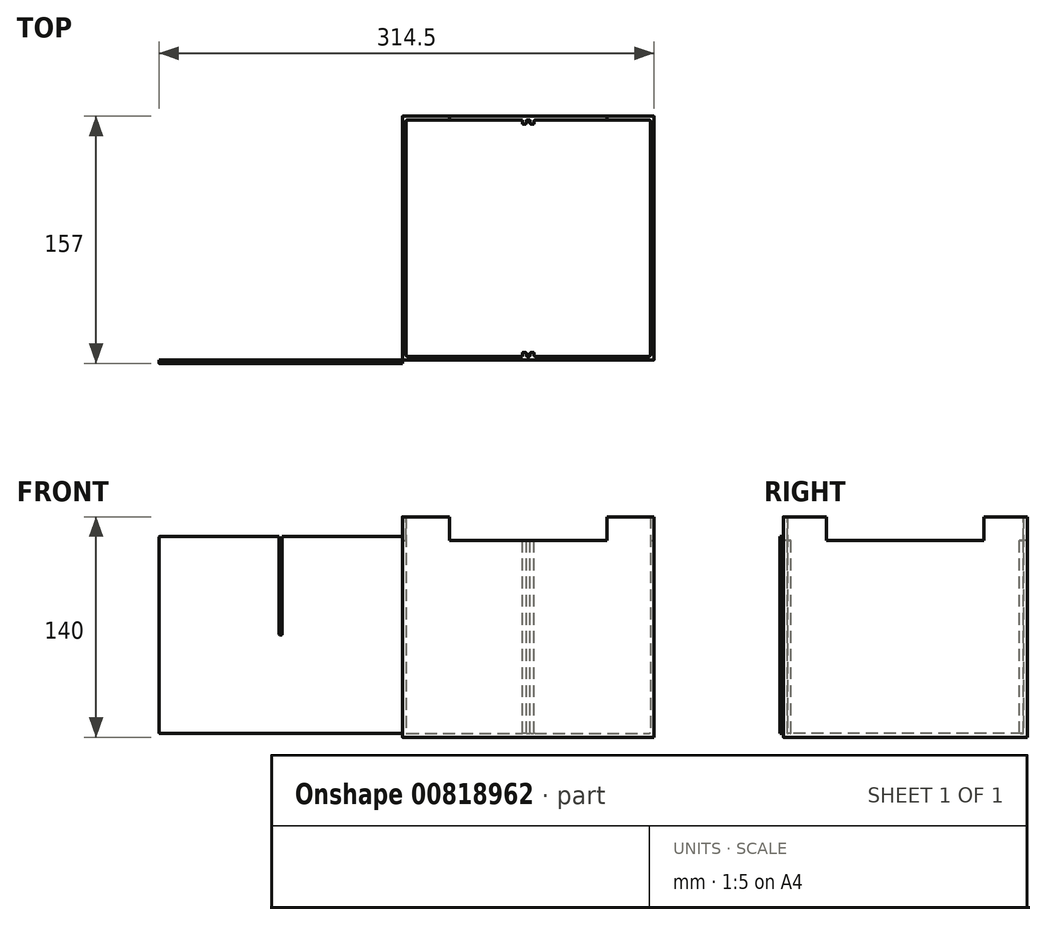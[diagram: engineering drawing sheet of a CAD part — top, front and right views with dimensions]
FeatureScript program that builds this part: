
annotation { "Feature Type Name" : "Feature", "Feature Type Description" : "" }
export const myFeature = defineFeature(function(context is Context, id is Id, definition is map)
    precondition{}
    {
        {
            var Q0;
            Q0=qCreatedBy(makeId("Top.planeOp"),FACE);
            var sketch = newSketch(context, id + "F0", { "sketchPlane" : qUnion([Q0])});
            skLineSegment(sketch, "E0.bottom", {"start": v(0, 0) * mm, "end": v(2.5, 0) * mm});
            skLineSegment(sketch, "E0.top", {"start": v(0, 155) * mm, "end": v(160, 155) * mm});
            skLineSegment(sketch, "E0.left", {"start": v(0, 0) * mm, "end": v(0, 155) * mm});
            skLineSegment(sketch, "E0.right", {"start": v(160, 0) * mm, "end": v(160, 155) * mm});
            skLineSegment(sketch, "E1.0", {"start": v(2.5, 152.5) * mm, "end": v(157.5, 152.5) * mm});
            skLineSegment(sketch, "E1.1", {"start": v(2.5, 2.5) * mm, "end": v(2.5, 152.5) * mm});
            skLineSegment(sketch, "E2", {"start": v(2.5, 2.5) * mm, "end": v(2.5, 0) * mm});
            skLineSegment(sketch, "E3.trimOffspring", {"start": v(157.5, 0) * mm, "end": v(160, 0) * mm});
            skLineSegment(sketch, "E4", {"start": v(157.5, 152.5) * mm, "end": v(157.5, 0) * mm});
            skLineSegment(sketch, "E5", {"start": v(2.5, 2.5) * mm, "end": v(157.5, 2.5) * mm});
            skLineSegment(sketch, "E6", {"start": v(2.5, 0) * mm, "end": v(157.5, 0) * mm});
            skSolve(sketch);
        }
        {
            var Q0;
            Q0=makeQuery(id+"F0.imprint","IMPRINT",FACE,{"disambiguationData":[TD([[makeQuery(id+"F0.imprint","IMPRINT",EDGE,{"derivedFrom":sQuery(id+"F0.wireOp",EDGE,"E0.bottom")}),1.0]])]});
            var Q1;
            Q1=makeQuery(id+"F0.imprint","IMPRINT",FACE,{"disambiguationData":[TD([[makeQuery(id+"F0.imprint","IMPRINT",EDGE,{"derivedFrom":sQuery(id+"F0.wireOp",EDGE,"E2")}),1.0]])]});
            extrude(context, id + "F1", {"entities" : qUnion([Q0, Q1]), "depth" : 137.5 * mm, "offsetDistance" : 25 * mm});
        }
        {
            var Q0;
            Q0=makeQuery(id+"F1.opExtrude","CAP_FACE",FACE,{"disambiguationData":[OSD([sQuery(id+"F0.wireOp",EDGE,"E0.bottom"),sQuery(id+"F0.wireOp",EDGE,"E0.top"),sQuery(id+"F0.wireOp",EDGE,"E0.left"),sQuery(id+"F0.wireOp",EDGE,"E0.right"),sQuery(id+"F0.wireOp",EDGE,"E1.0"),sQuery(id+"F0.wireOp",EDGE,"E1.1"),sQuery(id+"F0.wireOp",EDGE,"E2"),sQuery(id+"F0.wireOp",EDGE,"E3.trimOffspring"),sQuery(id+"F0.wireOp",EDGE,"E4")])],"isStart":true});
            var sketch = newSketch(context, id + "F2", { "sketchPlane" : qUnion([Q0])});
            skLineSegment(sketch, "E7.bottom", {"start": v(0, 0) * mm, "end": v(160, 0) * mm});
            skLineSegment(sketch, "E7.top", {"start": v(0, -155) * mm, "end": v(160, -155) * mm});
            skLineSegment(sketch, "E7.left", {"start": v(0, 0) * mm, "end": v(0, -155) * mm});
            skLineSegment(sketch, "E7.right", {"start": v(160, 0) * mm, "end": v(160, -155) * mm});
            skSolve(sketch);
        }
        {
            var Q0;
            Q0=makeQuery(id+"F2.imprint","IMPRINT",FACE,{"disambiguationData":[TD([[makeQuery(id+"F2.imprint","IMPRINT",EDGE,{"derivedFrom":makeQuery(id+"F1.opExtrude","CAP_EDGE",EDGE,{"disambiguationData":[OSD([sQuery(id+"F0.wireOp",EDGE,"E1.0")])],"isStart":true})}),1.0]])]});
            var Q1;
            Q1=makeQuery(id+"F2.imprint","IMPRINT",FACE,{"disambiguationData":[TD([[makeQuery(id+"F2.imprint","IMPRINT",EDGE,{"derivedFrom":sQuery(id+"F2.wireOp",EDGE,"E7.top")}),1.0]])]});
            extrude(context, id + "F3", {"entities" : qUnion([Q0, Q1]), "operationType" : NewBodyOperationType.ADD, "depth" : 2.5 * mm, "offsetDistance" : 25 * mm});
        }
        {
            var Q0;
            Q0=makeQuery(id+"F3.boolean.opBoolean","MERGE",EDGE,{"derivedFrom":[makeQuery(id+"F1.opExtrude","SWEPT_EDGE",EDGE,{"disambiguationData":[OSD([sQuery(id+"F0.wireOp",EDGE,"E0.top"),sQuery(id+"F0.wireOp",EDGE,"E0.left")])]}),makeQuery(id+"F3.opExtrude","SWEPT_EDGE",EDGE,{"disambiguationData":[OSD([sQuery(id+"F2.wireOp",EDGE,"E7.top"),sQuery(id+"F2.wireOp",EDGE,"E7.left")])]})]});
            var Q1;
            Q1=makeQuery(id+"F3.boolean.opBoolean","MERGE",EDGE,{"derivedFrom":[makeQuery(id+"F1.opExtrude","SWEPT_EDGE",EDGE,{"disambiguationData":[OSD([sQuery(id+"F0.wireOp",EDGE,"E0.top"),sQuery(id+"F0.wireOp",EDGE,"E0.right")])]}),makeQuery(id+"F3.opExtrude","SWEPT_EDGE",EDGE,{"disambiguationData":[OSD([sQuery(id+"F2.wireOp",EDGE,"E7.top"),sQuery(id+"F2.wireOp",EDGE,"E7.right")])]})]});
            var Q2;
            Q2=makeQuery(id+"F3.boolean.opBoolean","MERGE",EDGE,{"derivedFrom":[makeQuery(id+"F1.opExtrude","SWEPT_EDGE",EDGE,{"disambiguationData":[OSD([sQuery(id+"F0.wireOp",EDGE,"E0.right"),sQuery(id+"F0.wireOp",EDGE,"E3.trimOffspring")])]}),makeQuery(id+"F3.opExtrude","SWEPT_EDGE",EDGE,{"disambiguationData":[OSD([sQuery(id+"F2.wireOp",EDGE,"E7.bottom"),sQuery(id+"F2.wireOp",EDGE,"E7.right")])]})]});
            var Q3;
            Q3=makeQuery(id+"F3.boolean.opBoolean","MERGE",EDGE,{"derivedFrom":[makeQuery(id+"F1.opExtrude","SWEPT_EDGE",EDGE,{"disambiguationData":[OSD([sQuery(id+"F0.wireOp",EDGE,"E0.bottom"),sQuery(id+"F0.wireOp",EDGE,"E0.left")])]}),makeQuery(id+"F3.opExtrude","SWEPT_EDGE",EDGE,{"disambiguationData":[OSD([sQuery(id+"F2.wireOp",EDGE,"E7.bottom"),sQuery(id+"F2.wireOp",EDGE,"E7.left")])]})]});
            var Q4;
            Q4=makeQuery(id+"F1.opExtrude","SWEPT_EDGE",EDGE,{"disambiguationData":[OSD([sQuery(id+"F0.wireOp",EDGE,"E1.0"),sQuery(id+"F0.wireOp",EDGE,"E1.1")])]});
            var Q5;
            Q5=makeQuery(id+"F1.opExtrude","SWEPT_EDGE",EDGE,{"disambiguationData":[OSD([sQuery(id+"F0.wireOp",EDGE,"E1.0"),sQuery(id+"F0.wireOp",EDGE,"E4")])]});
            var Q6;
            Q6=makeQuery(id+"F1.opExtrude","SWEPT_EDGE",EDGE,{"disambiguationData":[OSD([sQuery(id+"F0.wireOp",EDGE,"E4"),sQuery(id+"F0.wireOp",EDGE,"E5")])]});
            var Q7;
            Q7=makeQuery(id+"F1.opExtrude","SWEPT_EDGE",EDGE,{"disambiguationData":[OSD([sQuery(id+"F0.wireOp",EDGE,"E1.1"),sQuery(id+"F0.wireOp",EDGE,"E2"),sQuery(id+"F0.wireOp",EDGE,"E5")])]});
            fillet(context, id + "F4", {"entities" : qUnion([Q0, Q1, Q2, Q3, Q4, Q5, Q6, Q7]), "radius" : 0.5 * mm, "tangentPropagation" : true, "allowEdgeOverflow" : false});
        }
        {
            var Q0;
            Q0=makeQuery(id+"F1.opExtrude","CAP_FACE",FACE,{"disambiguationData":[OSD([sQuery(id+"F0.wireOp",EDGE,"E0.bottom"),sQuery(id+"F0.wireOp",EDGE,"E0.top"),sQuery(id+"F0.wireOp",EDGE,"E0.left"),sQuery(id+"F0.wireOp",EDGE,"E0.right"),sQuery(id+"F0.wireOp",EDGE,"E1.0"),sQuery(id+"F0.wireOp",EDGE,"E1.1"),sQuery(id+"F0.wireOp",EDGE,"E3.trimOffspring"),sQuery(id+"F0.wireOp",EDGE,"E4"),sQuery(id+"F0.wireOp",EDGE,"E5"),sQuery(id+"F0.wireOp",EDGE,"E6")])],"isStart":false});
            var sketch = newSketch(context, id + "F5", { "sketchPlane" : qUnion([Q0])});
            skPoint(sketch, "E8", {"position": v(0, 77.5) * mm});
            skPoint(sketch, "E9", {"position": v(2.5, 77.5) * mm});
            skLineSegment(sketch, "E10.bottom", {"start": v(5, 78.75) * mm, "end": v(0, 78.75) * mm});
            skLineSegment(sketch, "E10.top", {"start": v(5, 76.25) * mm, "end": v(0, 76.25) * mm});
            skLineSegment(sketch, "E10.left", {"start": v(5, 78.75) * mm, "end": v(5, 76.25) * mm});
            skLineSegment(sketch, "E10.right", {"start": v(0, 78.75) * mm, "end": v(0, 76.25) * mm});
            skLineSegment(sketch, "E11.bottom", {"start": v(5, 78.75) * mm, "end": v(2.5, 78.75) * mm});
            skLineSegment(sketch, "E11.top", {"start": v(5, 81.25) * mm, "end": v(2.5, 81.25) * mm});
            skLineSegment(sketch, "E11.left", {"start": v(5, 78.75) * mm, "end": v(5, 81.25) * mm});
            skLineSegment(sketch, "E11.right", {"start": v(2.5, 78.75) * mm, "end": v(2.5, 81.25) * mm});
            skLineSegment(sketch, "E12.bottom", {"start": v(5, 76.25) * mm, "end": v(2.5, 76.25) * mm});
            skLineSegment(sketch, "E12.top", {"start": v(5, 73.75) * mm, "end": v(2.5, 73.75) * mm});
            skLineSegment(sketch, "E12.left", {"start": v(5, 76.25) * mm, "end": v(5, 73.75) * mm});
            skLineSegment(sketch, "E12.right", {"start": v(2.5, 76.25) * mm, "end": v(2.5, 73.75) * mm});
            skPoint(sketch, "E13", {"position": v(80, 152.5) * mm});
            skPoint(sketch, "E14", {"position": v(80, 155) * mm});
            skPoint(sketch, "E15", {"position": v(157.5, 77.5) * mm});
            skPoint(sketch, "E16", {"position": v(160, 77.5) * mm});
            skLineSegment(sketch, "E17.bottom", {"start": v(160, 78.75) * mm, "end": v(155, 78.75) * mm});
            skLineSegment(sketch, "E17.top", {"start": v(160, 76.25) * mm, "end": v(155, 76.25) * mm});
            skLineSegment(sketch, "E17.left", {"start": v(160, 78.75) * mm, "end": v(160, 76.25) * mm});
            skLineSegment(sketch, "E17.right", {"start": v(155, 78.75) * mm, "end": v(155, 76.25) * mm});
            skLineSegment(sketch, "E18.bottom", {"start": v(155, 78.75) * mm, "end": v(157.5, 78.75) * mm});
            skLineSegment(sketch, "E18.top", {"start": v(155, 81.25) * mm, "end": v(157.5, 81.25) * mm});
            skLineSegment(sketch, "E18.left", {"start": v(155, 78.75) * mm, "end": v(155, 81.25) * mm});
            skLineSegment(sketch, "E18.right", {"start": v(157.5, 78.75) * mm, "end": v(157.5, 81.25) * mm});
            skLineSegment(sketch, "E19.bottom", {"start": v(155, 76.25) * mm, "end": v(157.5, 76.25) * mm});
            skLineSegment(sketch, "E19.top", {"start": v(155, 73.75) * mm, "end": v(157.5, 73.75) * mm});
            skLineSegment(sketch, "E19.left", {"start": v(155, 76.25) * mm, "end": v(155, 73.75) * mm});
            skLineSegment(sketch, "E19.right", {"start": v(157.5, 76.25) * mm, "end": v(157.5, 73.75) * mm});
            skLineSegment(sketch, "E20.bottom", {"start": v(81.25, 155) * mm, "end": v(78.75, 155) * mm});
            skLineSegment(sketch, "E20.top", {"start": v(81.25, 150) * mm, "end": v(78.75, 150) * mm});
            skLineSegment(sketch, "E20.left", {"start": v(81.25, 155) * mm, "end": v(81.25, 150) * mm});
            skLineSegment(sketch, "E20.right", {"start": v(78.75, 155) * mm, "end": v(78.75, 150) * mm});
            skLineSegment(sketch, "E21.bottom", {"start": v(78.75, 150) * mm, "end": v(76.25, 150) * mm});
            skLineSegment(sketch, "E21.top", {"start": v(78.75, 152.5) * mm, "end": v(76.25, 152.5) * mm});
            skLineSegment(sketch, "E21.left", {"start": v(78.75, 150) * mm, "end": v(78.75, 152.5) * mm});
            skLineSegment(sketch, "E21.right", {"start": v(76.25, 150) * mm, "end": v(76.25, 152.5) * mm});
            skLineSegment(sketch, "E22.bottom", {"start": v(81.25, 150) * mm, "end": v(83.75, 150) * mm});
            skLineSegment(sketch, "E22.top", {"start": v(81.25, 152.5) * mm, "end": v(83.75, 152.5) * mm});
            skLineSegment(sketch, "E22.left", {"start": v(81.25, 150) * mm, "end": v(81.25, 152.5) * mm});
            skLineSegment(sketch, "E22.right", {"start": v(83.75, 150) * mm, "end": v(83.75, 152.5) * mm});
            skPoint(sketch, "E23", {"position": v(80, 2.5) * mm});
            skPoint(sketch, "E24", {"position": v(80, 0) * mm});
            skLineSegment(sketch, "E25.bottom", {"start": v(81.25, 0) * mm, "end": v(78.75, 0) * mm});
            skLineSegment(sketch, "E25.top", {"start": v(81.25, 5) * mm, "end": v(78.75, 5) * mm});
            skLineSegment(sketch, "E25.left", {"start": v(81.25, 0) * mm, "end": v(81.25, 5) * mm});
            skLineSegment(sketch, "E25.right", {"start": v(78.75, 0) * mm, "end": v(78.75, 5) * mm});
            skLineSegment(sketch, "E26.bottom", {"start": v(78.75, 5) * mm, "end": v(76.25, 5) * mm});
            skLineSegment(sketch, "E26.top", {"start": v(78.75, 2.5) * mm, "end": v(76.25, 2.5) * mm});
            skLineSegment(sketch, "E26.left", {"start": v(78.75, 5) * mm, "end": v(78.75, 2.5) * mm});
            skLineSegment(sketch, "E26.right", {"start": v(76.25, 5) * mm, "end": v(76.25, 2.5) * mm});
            skLineSegment(sketch, "E27.bottom", {"start": v(81.25, 5) * mm, "end": v(83.75, 5) * mm});
            skLineSegment(sketch, "E27.top", {"start": v(81.25, 2.5) * mm, "end": v(83.75, 2.5) * mm});
            skLineSegment(sketch, "E27.left", {"start": v(81.25, 5) * mm, "end": v(81.25, 2.5) * mm});
            skLineSegment(sketch, "E27.right", {"start": v(83.75, 5) * mm, "end": v(83.75, 2.5) * mm});
            skSolve(sketch);
        }
        {
            var Q0;
            Q0=makeQuery(id+"F5.imprint","IMPRINT",FACE,{"disambiguationData":[TD([[makeQuery(id+"F5.imprint","IMPRINT",EDGE,{"derivedFrom":sQuery(id+"F5.wireOp",EDGE,"E11.bottom")}),-1.0]])]});
            var Q1;
            Q1=makeQuery(id+"F5.imprint","IMPRINT",FACE,{"disambiguationData":[TD([[makeQuery(id+"F5.imprint","IMPRINT",EDGE,{"derivedFrom":sQuery(id+"F5.wireOp",EDGE,"E12.bottom")}),1.0]])]});
            var Q2;
            Q2=makeQuery(id+"F5.imprint","IMPRINT",FACE,{"disambiguationData":[TD([[makeQuery(id+"F5.imprint","IMPRINT",EDGE,{"derivedFrom":sQuery(id+"F5.wireOp",EDGE,"E26.bottom")}),1.0]])]});
            var Q3;
            Q3=makeQuery(id+"F5.imprint","IMPRINT",FACE,{"disambiguationData":[TD([[makeQuery(id+"F5.imprint","IMPRINT",EDGE,{"derivedFrom":sQuery(id+"F5.wireOp",EDGE,"E27.bottom")}),-1.0]])]});
            var Q4;
            Q4=makeQuery(id+"F5.imprint","IMPRINT",FACE,{"disambiguationData":[TD([[makeQuery(id+"F5.imprint","IMPRINT",EDGE,{"derivedFrom":sQuery(id+"F5.wireOp",EDGE,"E18.bottom")}),1.0]])]});
            var Q5;
            Q5=makeQuery(id+"F5.imprint","IMPRINT",FACE,{"disambiguationData":[TD([[makeQuery(id+"F5.imprint","IMPRINT",EDGE,{"derivedFrom":sQuery(id+"F5.wireOp",EDGE,"E19.bottom")}),-1.0]])]});
            var Q6;
            Q6=makeQuery(id+"F5.imprint","IMPRINT",FACE,{"disambiguationData":[TD([[makeQuery(id+"F5.imprint","IMPRINT",EDGE,{"derivedFrom":sQuery(id+"F5.wireOp",EDGE,"E22.bottom")}),1.0]])]});
            var Q7;
            Q7=makeQuery(id+"F5.imprint","IMPRINT",FACE,{"disambiguationData":[TD([[makeQuery(id+"F5.imprint","IMPRINT",EDGE,{"derivedFrom":sQuery(id+"F5.wireOp",EDGE,"E21.bottom")}),-1.0]])]});
            var Q8;
            Q8=makeQuery(id+"F3.opExtrude","CAP_FACE",FACE,{"disambiguationData":[OSD([sQuery(id+"F2.wireOp",EDGE,"E7.bottom"),sQuery(id+"F2.wireOp",EDGE,"E7.top"),sQuery(id+"F2.wireOp",EDGE,"E7.left"),sQuery(id+"F2.wireOp",EDGE,"E7.right")])],"isStart":true});
            extrude(context, id + "F6", {"entities" : qUnion([Q0, Q1, Q2, Q3, Q4, Q5, Q6, Q7]), "operationType" : NewBodyOperationType.ADD, "endBound" : BoundingType.UP_TO_SURFACE, "oppositeDirection" : true, "depth" : 25 * mm, "endBoundEntityFace" : qUnion([Q8]), "offsetDistance" : 25 * mm});
        }
        {
            var Q0;
            Q0=makeQuery(id+"F6.opExtrude","SWEPT_EDGE",EDGE,{"disambiguationData":[OSD([sQuery(id+"F5.wireOp",EDGE,"E11.top"),sQuery(id+"F5.wireOp",EDGE,"E11.left")])]});
            var Q1;
            Q1=makeQuery(id+"F6.opExtrude","SWEPT_EDGE",EDGE,{"disambiguationData":[OSD([sQuery(id+"F5.wireOp",EDGE,"E10.left"),sQuery(id+"F5.wireOp",EDGE,"E11.bottom"),sQuery(id+"F5.wireOp",EDGE,"E11.left")])]});
            var Q2;
            Q2=makeQuery(id+"F6.opExtrude","SWEPT_EDGE",EDGE,{"disambiguationData":[OSD([sQuery(id+"F0.wireOp",EDGE,"E1.1"),sQuery(id+"F5.wireOp",EDGE,"E10.bottom"),sQuery(id+"F5.wireOp",EDGE,"E11.bottom"),sQuery(id+"F5.wireOp",EDGE,"E11.right")])]});
            var Q3;
            Q3=makeQuery(id+"F6.opExtrude","SWEPT_EDGE",EDGE,{"disambiguationData":[OSD([sQuery(id+"F0.wireOp",EDGE,"E1.1"),sQuery(id+"F5.wireOp",EDGE,"E10.top"),sQuery(id+"F5.wireOp",EDGE,"E12.bottom"),sQuery(id+"F5.wireOp",EDGE,"E12.right")])]});
            var Q4;
            Q4=makeQuery(id+"F6.opExtrude","SWEPT_EDGE",EDGE,{"disambiguationData":[OSD([sQuery(id+"F5.wireOp",EDGE,"E10.left"),sQuery(id+"F5.wireOp",EDGE,"E12.bottom"),sQuery(id+"F5.wireOp",EDGE,"E12.left")])]});
            var Q5;
            Q5=makeQuery(id+"F6.opExtrude","SWEPT_EDGE",EDGE,{"disambiguationData":[OSD([sQuery(id+"F5.wireOp",EDGE,"E12.top"),sQuery(id+"F5.wireOp",EDGE,"E12.left")])]});
            var Q6;
            Q6=makeQuery(id+"F6.opExtrude","SWEPT_EDGE",EDGE,{"disambiguationData":[OSD([sQuery(id+"F0.wireOp",EDGE,"E1.1"),sQuery(id+"F5.wireOp",EDGE,"E12.top"),sQuery(id+"F5.wireOp",EDGE,"E12.right")])]});
            var Q7;
            Q7=makeQuery(id+"F6.opExtrude","SWEPT_EDGE",EDGE,{"disambiguationData":[OSD([sQuery(id+"F0.wireOp",EDGE,"E1.1"),sQuery(id+"F5.wireOp",EDGE,"E11.top"),sQuery(id+"F5.wireOp",EDGE,"E11.right")])]});
            var Q8;
            Q8=makeQuery(id+"F6.opExtrude","SWEPT_EDGE",EDGE,{"disambiguationData":[OSD([sQuery(id+"F5.wireOp",EDGE,"E21.bottom"),sQuery(id+"F5.wireOp",EDGE,"E21.right")])]});
            var Q9;
            Q9=makeQuery(id+"F6.opExtrude","SWEPT_EDGE",EDGE,{"disambiguationData":[OSD([sQuery(id+"F5.wireOp",EDGE,"E20.top"),sQuery(id+"F5.wireOp",EDGE,"E21.bottom"),sQuery(id+"F5.wireOp",EDGE,"E21.left")])]});
            var Q10;
            Q10=makeQuery(id+"F6.opExtrude","SWEPT_EDGE",EDGE,{"disambiguationData":[OSD([sQuery(id+"F0.wireOp",EDGE,"E1.0"),sQuery(id+"F5.wireOp",EDGE,"E20.right"),sQuery(id+"F5.wireOp",EDGE,"E21.top"),sQuery(id+"F5.wireOp",EDGE,"E21.left")])]});
            var Q11;
            Q11=makeQuery(id+"F6.opExtrude","SWEPT_EDGE",EDGE,{"disambiguationData":[OSD([sQuery(id+"F0.wireOp",EDGE,"E1.0"),sQuery(id+"F5.wireOp",EDGE,"E20.left"),sQuery(id+"F5.wireOp",EDGE,"E22.top"),sQuery(id+"F5.wireOp",EDGE,"E22.left")])]});
            var Q12;
            Q12=makeQuery(id+"F6.opExtrude","SWEPT_EDGE",EDGE,{"disambiguationData":[OSD([sQuery(id+"F5.wireOp",EDGE,"E20.top"),sQuery(id+"F5.wireOp",EDGE,"E22.bottom"),sQuery(id+"F5.wireOp",EDGE,"E22.left")])]});
            var Q13;
            Q13=makeQuery(id+"F6.opExtrude","SWEPT_EDGE",EDGE,{"disambiguationData":[OSD([sQuery(id+"F5.wireOp",EDGE,"E22.bottom"),sQuery(id+"F5.wireOp",EDGE,"E22.right")])]});
            var Q14;
            Q14=makeQuery(id+"F6.opExtrude","SWEPT_EDGE",EDGE,{"disambiguationData":[OSD([sQuery(id+"F0.wireOp",EDGE,"E1.0"),sQuery(id+"F5.wireOp",EDGE,"E22.top"),sQuery(id+"F5.wireOp",EDGE,"E22.right")])]});
            var Q15;
            Q15=makeQuery(id+"F6.opExtrude","SWEPT_EDGE",EDGE,{"disambiguationData":[OSD([sQuery(id+"F0.wireOp",EDGE,"E1.0"),sQuery(id+"F5.wireOp",EDGE,"E21.top"),sQuery(id+"F5.wireOp",EDGE,"E21.right")])]});
            var Q16;
            Q16=makeQuery(id+"F6.opExtrude","SWEPT_EDGE",EDGE,{"disambiguationData":[OSD([sQuery(id+"F0.wireOp",EDGE,"E4"),sQuery(id+"F5.wireOp",EDGE,"E19.top"),sQuery(id+"F5.wireOp",EDGE,"E19.right")])]});
            var Q17;
            Q17=makeQuery(id+"F6.opExtrude","SWEPT_EDGE",EDGE,{"disambiguationData":[OSD([sQuery(id+"F5.wireOp",EDGE,"E19.top"),sQuery(id+"F5.wireOp",EDGE,"E19.left")])]});
            var Q18;
            Q18=makeQuery(id+"F6.opExtrude","SWEPT_EDGE",EDGE,{"disambiguationData":[OSD([sQuery(id+"F5.wireOp",EDGE,"E17.right"),sQuery(id+"F5.wireOp",EDGE,"E19.bottom"),sQuery(id+"F5.wireOp",EDGE,"E19.left")])]});
            var Q19;
            Q19=makeQuery(id+"F6.opExtrude","SWEPT_EDGE",EDGE,{"disambiguationData":[OSD([sQuery(id+"F0.wireOp",EDGE,"E4"),sQuery(id+"F5.wireOp",EDGE,"E18.top"),sQuery(id+"F5.wireOp",EDGE,"E18.right")])]});
            var Q20;
            Q20=makeQuery(id+"F6.opExtrude","SWEPT_EDGE",EDGE,{"disambiguationData":[OSD([sQuery(id+"F5.wireOp",EDGE,"E18.top"),sQuery(id+"F5.wireOp",EDGE,"E18.left")])]});
            var Q21;
            Q21=makeQuery(id+"F6.opExtrude","SWEPT_EDGE",EDGE,{"disambiguationData":[OSD([sQuery(id+"F5.wireOp",EDGE,"E17.right"),sQuery(id+"F5.wireOp",EDGE,"E18.bottom"),sQuery(id+"F5.wireOp",EDGE,"E18.left")])]});
            var Q22;
            Q22=makeQuery(id+"F6.opExtrude","SWEPT_EDGE",EDGE,{"disambiguationData":[OSD([sQuery(id+"F0.wireOp",EDGE,"E4"),sQuery(id+"F5.wireOp",EDGE,"E17.bottom"),sQuery(id+"F5.wireOp",EDGE,"E18.bottom"),sQuery(id+"F5.wireOp",EDGE,"E18.right")])]});
            var Q23;
            Q23=makeQuery(id+"F6.opExtrude","SWEPT_EDGE",EDGE,{"disambiguationData":[OSD([sQuery(id+"F0.wireOp",EDGE,"E4"),sQuery(id+"F5.wireOp",EDGE,"E17.top"),sQuery(id+"F5.wireOp",EDGE,"E19.bottom"),sQuery(id+"F5.wireOp",EDGE,"E19.right")])]});
            var Q24;
            Q24=makeQuery(id+"F6.opExtrude","SWEPT_EDGE",EDGE,{"disambiguationData":[OSD([sQuery(id+"F0.wireOp",EDGE,"E5"),sQuery(id+"F5.wireOp",EDGE,"E26.top"),sQuery(id+"F5.wireOp",EDGE,"E26.right")])]});
            var Q25;
            Q25=makeQuery(id+"F6.opExtrude","SWEPT_EDGE",EDGE,{"disambiguationData":[OSD([sQuery(id+"F5.wireOp",EDGE,"E26.bottom"),sQuery(id+"F5.wireOp",EDGE,"E26.right")])]});
            var Q26;
            Q26=makeQuery(id+"F6.opExtrude","SWEPT_EDGE",EDGE,{"disambiguationData":[OSD([sQuery(id+"F5.wireOp",EDGE,"E25.top"),sQuery(id+"F5.wireOp",EDGE,"E26.bottom"),sQuery(id+"F5.wireOp",EDGE,"E26.left")])]});
            var Q27;
            Q27=makeQuery(id+"F6.opExtrude","SWEPT_EDGE",EDGE,{"disambiguationData":[OSD([sQuery(id+"F0.wireOp",EDGE,"E5"),sQuery(id+"F5.wireOp",EDGE,"E25.right"),sQuery(id+"F5.wireOp",EDGE,"E26.top"),sQuery(id+"F5.wireOp",EDGE,"E26.left")])]});
            var Q28;
            Q28=makeQuery(id+"F6.opExtrude","SWEPT_EDGE",EDGE,{"disambiguationData":[OSD([sQuery(id+"F5.wireOp",EDGE,"E25.top"),sQuery(id+"F5.wireOp",EDGE,"E27.bottom"),sQuery(id+"F5.wireOp",EDGE,"E27.left")])]});
            var Q29;
            Q29=makeQuery(id+"F6.opExtrude","SWEPT_EDGE",EDGE,{"disambiguationData":[OSD([sQuery(id+"F0.wireOp",EDGE,"E5"),sQuery(id+"F5.wireOp",EDGE,"E25.left"),sQuery(id+"F5.wireOp",EDGE,"E27.top"),sQuery(id+"F5.wireOp",EDGE,"E27.left")])]});
            var Q30;
            Q30=makeQuery(id+"F6.opExtrude","SWEPT_EDGE",EDGE,{"disambiguationData":[OSD([sQuery(id+"F0.wireOp",EDGE,"E5"),sQuery(id+"F5.wireOp",EDGE,"E27.top"),sQuery(id+"F5.wireOp",EDGE,"E27.right")])]});
            var Q31;
            Q31=makeQuery(id+"F6.opExtrude","SWEPT_EDGE",EDGE,{"disambiguationData":[OSD([sQuery(id+"F5.wireOp",EDGE,"E27.bottom"),sQuery(id+"F5.wireOp",EDGE,"E27.right")])]});
            fillet(context, id + "F7", {"entities" : qUnion([Q0, Q1, Q2, Q3, Q4, Q5, Q6, Q7, Q8, Q9, Q10, Q11, Q12, Q13, Q14, Q15, Q16, Q17, Q18, Q19, Q20, Q21, Q22, Q23, Q24, Q25, Q26, Q27, Q28, Q29, Q30, Q31]), "radius" : 0.5 * mm, "tangentPropagation" : true, "allowEdgeOverflow" : false});
        }
        {
            var Q0;
            Q0=qCreatedBy(makeId("Front.planeOp"),FACE);
            var sketch = newSketch(context, id + "F8", { "sketchPlane" : qUnion([Q0])});
            skLineSegment(sketch, "E28.bottom", {"start": v(0, 0) * mm, "end": v(-154.5, 0) * mm});
            skLineSegment(sketch, "E28.top", {"start": v(0, 125) * mm, "end": v(-154.5, 125) * mm});
            skLineSegment(sketch, "E28.left", {"start": v(0, 0) * mm, "end": v(0, 125) * mm});
            skLineSegment(sketch, "E28.right", {"start": v(-154.5, 0) * mm, "end": v(-154.5, 125) * mm});
            skSolve(sketch);
        }
        {
            var Q0;
            Q0=makeQuery(id+"F8.imprint","IMPRINT",FACE,{"disambiguationData":[TD([[makeQuery(id+"F8.imprint","IMPRINT",EDGE,{"derivedFrom":sQuery(id+"F8.wireOp",EDGE,"E28.bottom")}),-1.0]])]});
            extrude(context, id + "F9", {"entities" : qUnion([Q0]), "depth" : 2 * mm, "offsetDistance" : 25 * mm});
        }
        {
            var Q0;
            Q0=makeQuery(id+"F9.opExtrude","SWEPT_EDGE",EDGE,{"disambiguationData":[OSD([sQuery(id+"F8.wireOp",EDGE,"E28.bottom"),sQuery(id+"F8.wireOp",EDGE,"E28.left")])]});
            var Q1;
            Q1=makeQuery(id+"F9.opExtrude","SWEPT_EDGE",EDGE,{"disambiguationData":[OSD([sQuery(id+"F8.wireOp",EDGE,"E28.top"),sQuery(id+"F8.wireOp",EDGE,"E28.left")])]});
            var Q2;
            Q2=makeQuery(id+"F9.opExtrude","SWEPT_EDGE",EDGE,{"disambiguationData":[OSD([sQuery(id+"F8.wireOp",EDGE,"E28.top"),sQuery(id+"F8.wireOp",EDGE,"E28.right")])]});
            var Q3;
            Q3=makeQuery(id+"F9.opExtrude","SWEPT_EDGE",EDGE,{"disambiguationData":[OSD([sQuery(id+"F8.wireOp",EDGE,"E28.bottom"),sQuery(id+"F8.wireOp",EDGE,"E28.right")])]});
            fillet(context, id + "F10", {"entities" : qUnion([Q0, Q1, Q2, Q3]), "radius" : 0.5 * mm, "tangentPropagation" : true, "allowEdgeOverflow" : false});
        }
        {
            var Q0;
            Q0=makeQuery(id+"F9.opExtrude","SWEPT_BODY",BODY,{"disambiguationData":[OSD([sQuery(id+"F8.wireOp",EDGE,"E28.bottom"),sQuery(id+"F8.wireOp",EDGE,"E28.top"),sQuery(id+"F8.wireOp",EDGE,"E28.left"),sQuery(id+"F8.wireOp",EDGE,"E28.right")])]});
            transform(context, id + "F11", {"entities" : qUnion([Q0]), "transformType" : TransformType.TRANSLATION_3D, "dx" : 0 * mm, "dy" : 0 * mm, "dz" : 0 * mm, "makeCopy" : true});
        }
        {
            var Q0;
            Q0=makeQuery(id+"F9.opExtrude","SWEPT_BODY",BODY,{"disambiguationData":[OSD([sQuery(id+"F8.wireOp",EDGE,"E28.bottom"),sQuery(id+"F8.wireOp",EDGE,"E28.top"),sQuery(id+"F8.wireOp",EDGE,"E28.left"),sQuery(id+"F8.wireOp",EDGE,"E28.right")])]});
            var Q1;
            {var subQ0=sQuery(id+"F2.wireOp",EDGE,"E7.left");var subQ1=sQuery(id+"F0.wireOp",EDGE,"E0.left");Q1=makeQuery(id+"F4.opFillet","BLEND_EDGE",EDGE,{"blendedFrom":[makeQuery(id+"F3.boolean.opBoolean","MERGE",EDGE,{"derivedFrom":[makeQuery(id+"F1.opExtrude","SWEPT_EDGE",EDGE,{"disambiguationData":[OSD([sQuery(id+"F0.wireOp",EDGE,"E0.top"),subQ1])]}),makeQuery(id+"F3.opExtrude","SWEPT_EDGE",EDGE,{"disambiguationData":[OSD([sQuery(id+"F2.wireOp",EDGE,"E7.top"),subQ0])]})]}),makeQuery(id+"F3.boolean.opBoolean","MERGE",FACE,{"derivedFrom":[makeQuery(id+"F1.opExtrude","SWEPT_FACE",FACE,{"disambiguationData":[OSD([subQ1])]}),makeQuery(id+"F3.opExtrude","SWEPT_FACE",FACE,{"disambiguationData":[OSD([subQ0])]})]})],"blendedInto":[makeQuery(id+"F3.boolean.opBoolean","MERGE",FACE,{"derivedFrom":[makeQuery(id+"F1.opExtrude","SWEPT_FACE",FACE,{"disambiguationData":[OSD([subQ1])]}),makeQuery(id+"F3.opExtrude","SWEPT_FACE",FACE,{"disambiguationData":[OSD([subQ0])]})]})]});}
            transform(context, id + "F12", {"entities" : qUnion([Q0]), "transformType" : TransformType.ROTATION, "transformAxis" : qUnion([Q1]), "angle" : 90 * degree, "makeCopy" : true});
        }
        {
            var Q0;
            Q0=makeQuery(id+"F12.opPattern","COPY",BODY,{"derivedFrom":makeQuery(id+"F9.opExtrude","SWEPT_BODY",BODY,{"disambiguationData":[OSD([sQuery(id+"F8.wireOp",EDGE,"E28.bottom"),sQuery(id+"F8.wireOp",EDGE,"E28.top"),sQuery(id+"F8.wireOp",EDGE,"E28.left"),sQuery(id+"F8.wireOp",EDGE,"E28.right")])]}),"instanceName":"1"});
            deleteBodies(context, id + "F13", {"entities" : qUnion([Q0])});
        }
        {
            var Q0;
            Q0=makeQuery(id+"F11.opPattern","COPY",BODY,{"derivedFrom":makeQuery(id+"F9.opExtrude","SWEPT_BODY",BODY,{"disambiguationData":[OSD([sQuery(id+"F8.wireOp",EDGE,"E28.bottom"),sQuery(id+"F8.wireOp",EDGE,"E28.top"),sQuery(id+"F8.wireOp",EDGE,"E28.left"),sQuery(id+"F8.wireOp",EDGE,"E28.right")])]}),"instanceName":"1"});
            deleteBodies(context, id + "F14", {"entities" : qUnion([Q0])});
        }
        {
            var Q0;
            Q0=makeQuery(id+"F9.opExtrude","CAP_FACE",FACE,{"disambiguationData":[OSD([sQuery(id+"F8.wireOp",EDGE,"E28.bottom"),sQuery(id+"F8.wireOp",EDGE,"E28.top"),sQuery(id+"F8.wireOp",EDGE,"E28.left"),sQuery(id+"F8.wireOp",EDGE,"E28.right")])],"isStart":false});
            var sketch = newSketch(context, id + "F15", { "sketchPlane" : qUnion([Q0])});
            skPoint(sketch, "E29", {"position": v(-77.25, 125) * mm});
            skPoint(sketch, "E30", {"position": v(-154.5, 62.5) * mm});
            skPoint(sketch, "E31", {"position": v(-78.25, 125) * mm});
            skPoint(sketch, "E32", {"position": v(-76.25, 125) * mm});
            skLineSegment(sketch, "E33", {"start": v(-154.5, 62.5) * mm, "end": v(0, 62.5) * mm, "construction": true});
            skLineSegment(sketch, "E34", {"start": v(-78.25, 125) * mm, "end": v(-78.25, 62.5) * mm});
            skLineSegment(sketch, "E35", {"start": v(-76.25, 125) * mm, "end": v(-76.25, 62.5) * mm});
            skLineSegment(sketch, "E36", {"start": v(-78.25, 62.5) * mm, "end": v(-76.25, 62.5) * mm});
            skSolve(sketch);
        }
        {
            var Q0;
            {var subQ0=sQuery(id+"F15.wireOp",EDGE,"E34");Q0=makeQuery(id+"F15.imprint","IMPRINT",FACE,{"disambiguationData":[TD([[makeQuery(id+"F15.imprint","IMPRINT",EDGE,{"derivedFrom":subQ0}),1.0]])]});}
            extrude(context, id + "F16", {"entities" : qUnion([Q0]), "operationType" : NewBodyOperationType.REMOVE, "endBound" : BoundingType.THROUGH_ALL, "oppositeDirection" : true, "depth" : 25 * mm, "offsetDistance" : 25 * mm});
        }
        {
            var Q0;
            Q0=makeQuery(id+"F16.boolean.opBoolean","COPY",EDGE,{"derivedFrom":makeQuery(id+"F16.opExtrude","SWEPT_EDGE",EDGE,{"disambiguationData":[OSD([sQuery(id+"F15.wireOp",EDGE,"E34"),sQuery(id+"F15.wireOp",EDGE,"E36")])]})});
            var Q1;
            Q1=makeQuery(id+"F16.boolean.opBoolean","COPY",EDGE,{"derivedFrom":makeQuery(id+"F16.opExtrude","SWEPT_EDGE",EDGE,{"disambiguationData":[OSD([sQuery(id+"F15.wireOp",EDGE,"E35"),sQuery(id+"F15.wireOp",EDGE,"E36")])]})});
            fillet(context, id + "F17", {"entities" : qUnion([Q0, Q1]), "radius" : 0.5 * mm, "tangentPropagation" : true, "allowEdgeOverflow" : false});
        }
        {
            var Q0;
            Q0=makeQuery(id+"F3.boolean.opBoolean","MERGE",FACE,{"derivedFrom":[makeQuery(id+"F1.opExtrude","SWEPT_FACE",FACE,{"disambiguationData":[OSD([sQuery(id+"F0.wireOp",EDGE,"E0.bottom"),sQuery(id+"F0.wireOp",EDGE,"E3.trimOffspring"),sQuery(id+"F0.wireOp",EDGE,"E6")])]}),makeQuery(id+"F3.opExtrude","SWEPT_FACE",FACE,{"disambiguationData":[OSD([sQuery(id+"F2.wireOp",EDGE,"E7.bottom")])]})]});
            var sketch = newSketch(context, id + "F18", { "sketchPlane" : qUnion([Q0])});
            skLineSegment(sketch, "E37.bottom", {"start": v(30, 137.5) * mm, "end": v(130, 137.5) * mm});
            skLineSegment(sketch, "E37.top", {"start": v(30, 122.5) * mm, "end": v(130, 122.5) * mm});
            skLineSegment(sketch, "E37.left", {"start": v(30, 137.5) * mm, "end": v(30, 122.5) * mm});
            skLineSegment(sketch, "E37.right", {"start": v(130, 137.5) * mm, "end": v(130, 122.5) * mm});
            skSolve(sketch);
        }
        {
            var Q0;
            Q0=makeQuery(id+"F18.imprint","IMPRINT",FACE,{"disambiguationData":[TD([[makeQuery(id+"F18.imprint","IMPRINT",EDGE,{"derivedFrom":sQuery(id+"F18.wireOp",EDGE,"E37.bottom")}),-1.0]])]});
            extrude(context, id + "F19", {"entities" : qUnion([Q0]), "operationType" : NewBodyOperationType.REMOVE, "endBound" : BoundingType.THROUGH_ALL, "oppositeDirection" : true, "depth" : 25 * mm, "offsetDistance" : 25 * mm});
        }
        {
            var Q0;
            Q0=makeQuery(id+"F3.boolean.opBoolean","MERGE",FACE,{"derivedFrom":[makeQuery(id+"F1.opExtrude","SWEPT_FACE",FACE,{"disambiguationData":[OSD([sQuery(id+"F0.wireOp",EDGE,"E0.right")])]}),makeQuery(id+"F3.opExtrude","SWEPT_FACE",FACE,{"disambiguationData":[OSD([sQuery(id+"F2.wireOp",EDGE,"E7.right")])]})]});
            var sketch = newSketch(context, id + "F20", { "sketchPlane" : qUnion([Q0])});
            skLineSegment(sketch, "E38.bottom", {"start": v(27.5, 137.5) * mm, "end": v(127.5, 137.5) * mm});
            skLineSegment(sketch, "E38.top", {"start": v(27.5, 122.5) * mm, "end": v(127.5, 122.5) * mm});
            skLineSegment(sketch, "E38.left", {"start": v(27.5, 137.5) * mm, "end": v(27.5, 122.5) * mm});
            skLineSegment(sketch, "E38.right", {"start": v(127.5, 137.5) * mm, "end": v(127.5, 122.5) * mm});
            skSolve(sketch);
        }
        {
            var Q0;
            Q0=makeQuery(id+"F20.imprint","IMPRINT",FACE,{"disambiguationData":[TD([[makeQuery(id+"F20.imprint","IMPRINT",EDGE,{"derivedFrom":sQuery(id+"F20.wireOp",EDGE,"E38.bottom")}),-1.0]])]});
            extrude(context, id + "F21", {"entities" : qUnion([Q0]), "operationType" : NewBodyOperationType.REMOVE, "endBound" : BoundingType.THROUGH_ALL, "oppositeDirection" : true, "depth" : 25 * mm, "offsetDistance" : 25 * mm});
        }
    });
